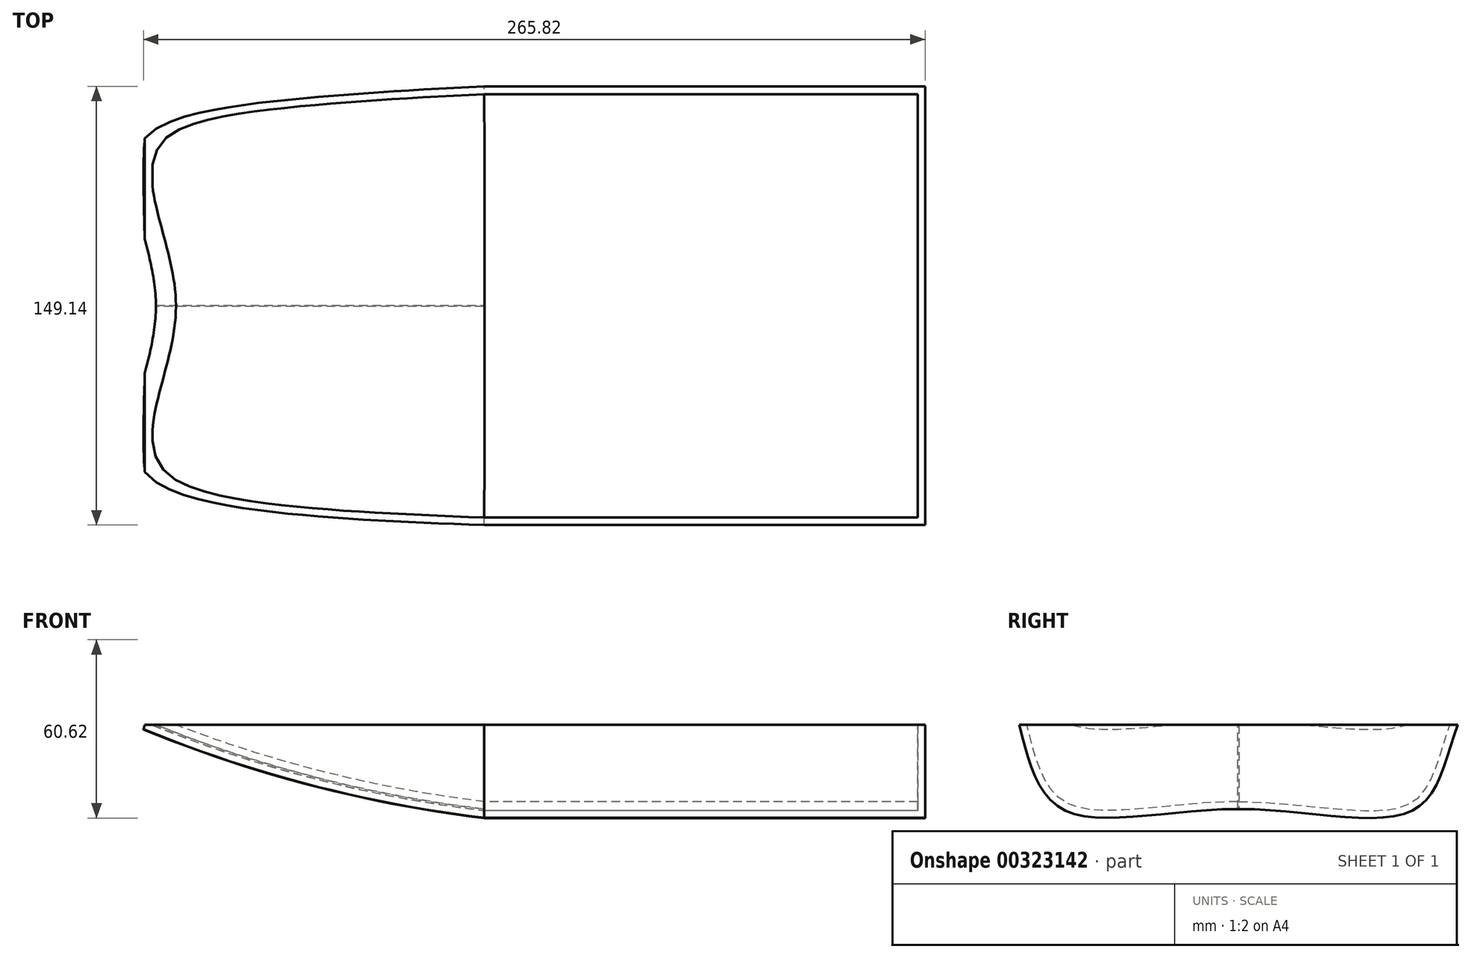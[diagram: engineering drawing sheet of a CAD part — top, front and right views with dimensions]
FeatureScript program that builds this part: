
annotation { "Feature Type Name" : "Feature", "Feature Type Description" : "" }
export const myFeature = defineFeature(function(context is Context, id is Id, definition is map)
    precondition{}
    {
        {
            var Q0;
            Q0=qCreatedBy(makeId("Front.planeOp"),FACE);
            var sketch = newSketch(context, id + "F0", { "sketchPlane" : qUnion([Q0])});
            skLineSegment(sketch, "E0.bottom", {"start": v(0, 0) * mm, "end": v(150, 0) * mm});
            skLineSegment(sketch, "E0.right", {"start": v(150, 0) * mm, "end": v(150, 30) * mm});
            skArc(sketch, "E1", {"start": v(-115, 30) * mm, "mid": v(-58.52, 11.1) * mm, "end": v(0, 0) * mm});
            skPoint(sketch, "E2.top.end.orphan", {"position": v(-115, 0) * mm});
            skSolve(sketch);
        }
        {
            var Q0;
            Q0=qCreatedBy(makeId("Right.planeOp"),FACE);
            cPlane(context, id + "F1", {"entities" : qUnion([Q0]), "cplaneType" : CPlaneType.OFFSET, "offset" : 150 * mm, "width" : 150 * mm, "height" : 150 * mm});
        }
        {
            var Q0;
            Q0=qCreatedBy(id+"F1.planeOp",FACE);
            var sketch = newSketch(context, id + "F2", { "sketchPlane" : qUnion([Q0])});
            skLineSegment(sketch, "E3.bottom", {"start": v(-75, 30) * mm, "end": v(75, 30) * mm});
            skLineSegment(sketch, "E3.top", {"start": v(-0.31, 0) * mm, "end": v(0, 0) * mm});
            skFitSpline(sketch, "E4", {"points": [v(-75, 30) * mm, v(-60, 0) * mm, v(0, 0) * mm, v(60, 0) * mm, v(75, 30) * mm], "startDerivative": vector(43.02, -173.66) * mm, "endDerivative": vector(65.03, 169.84) * mm});
            skPoint(sketch, "E5.orphan", {"position": v(-75, 0) * mm});
            skPoint(sketch, "E3.right.end.orphan", {"position": v(75, 0) * mm});
            skSolve(sketch);
        }
        {
            var Q0;
            {var subQ0=sQuery(id+"F2.wireOp",EDGE,"E3.bottom");Q0=makeQuery(id+"F2.imprint","IMPRINT",FACE,{"disambiguationData":[TD([[makeQuery(id+"F2.imprint","IMPRINT",EDGE,{"derivedFrom":subQ0}),-1.0]])]});}
            extrude(context, id + "F3", {"entities" : qUnion([Q0]), "oppositeDirection" : true, "depth" : 150 * mm});
        }
        {
            var Q0;
            Q0=makeQuery(id+"F3.opExtrude","CAP_FACE",FACE,{"disambiguationData":[OSD([sQuery(id+"F2.wireOp",EDGE,"E3.bottom"),sQuery(id+"F2.wireOp",EDGE,"E4")])],"isStart":false});
            var Q1;
            Q1=qSketchRegion(id+"F0",true);
            var Q2;
            Q2=sQuery(id+"F0.wireOp",EDGE,"E1");
            sweep(context, id + "F4", {"operationType" : NewBodyOperationType.ADD, "profiles" : qUnion([Q0, Q1]), "path" : qUnion([Q2])});
        }
        {
            var Q0;
            Q0=qCreatedBy(makeId("Front.planeOp"),FACE);
            var sketch = newSketch(context, id + "F5", { "sketchPlane" : qUnion([Q0])});
            skLineSegment(sketch, "E6.bottom", {"start": v(154.83, 28.62) * mm, "end": v(-132.64, 28.62) * mm});
            skLineSegment(sketch, "E6.top", {"start": v(154.83, 68.12) * mm, "end": v(-132.64, 68.12) * mm});
            skLineSegment(sketch, "E6.left", {"start": v(154.83, 28.62) * mm, "end": v(154.83, 68.12) * mm});
            skLineSegment(sketch, "E6.right", {"start": v(-132.64, 28.62) * mm, "end": v(-132.64, 68.12) * mm});
            skSolve(sketch);
        }
        {
            var Q0;
            Q0=qSketchRegion(id+"F5",true);
            extrude(context, id + "F6", {"entities" : qUnion([Q0]), "operationType" : NewBodyOperationType.REMOVE, "endBound" : BoundingType.SYMMETRIC, "oppositeDirection" : true, "depth" : 200 * mm});
        }
        {
            var Q0;
            Q0=makeQuery(id+"F6.boolean.opBoolean","COPY",FACE,{"derivedFrom":makeQuery(id+"F6.opExtrude","SWEPT_FACE",FACE,{"disambiguationData":[OSD([sQuery(id+"F5.wireOp",EDGE,"E6.bottom")])]})});
            var Q1;
            Q1=makeQuery(id+"F3.opExtrude","SWEPT_BODY",BODY,{"disambiguationData":[OSD([sQuery(id+"F2.wireOp",EDGE,"E3.bottom"),sQuery(id+"F2.wireOp",EDGE,"E4")])]});
            shell(context, id + "F7", {"entities" : qUnion([Q0]), "parts" : qUnion([Q1]), "thickness" : 2.5 * mm});
        }
    });
